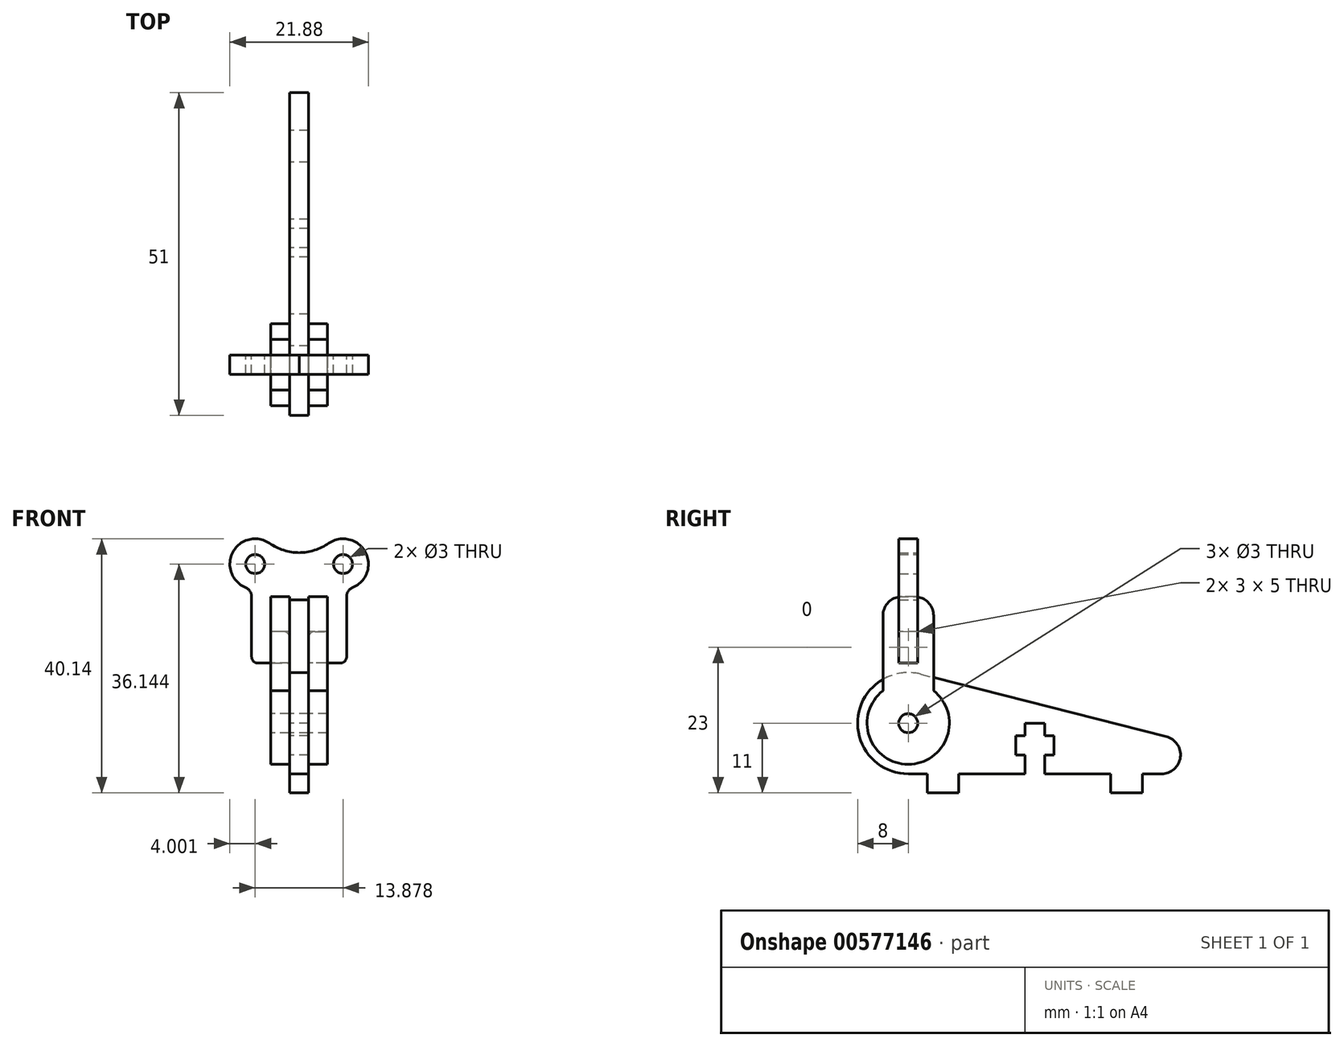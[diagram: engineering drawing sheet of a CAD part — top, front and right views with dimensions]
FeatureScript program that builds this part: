
annotation { "Feature Type Name" : "Feature", "Feature Type Description" : "" }
export const myFeature = defineFeature(function(context is Context, id is Id, definition is map)
    precondition{}
    {
        {
            var Q0;
            Q0=qCreatedBy(makeId("Right.planeOp"),FACE);
            var sketch = newSketch(context, id + "F0", { "sketchPlane" : qUnion([Q0])});
            skLineSegment(sketch, "E0", {"start": v(-20, 0) * mm, "end": v(-17, 0) * mm});
            skLineSegment(sketch, "E1", {"start": v(-17, 0) * mm, "end": v(-17, -3) * mm});
            skLineSegment(sketch, "E2", {"start": v(-17, -3) * mm, "end": v(-12, -3) * mm});
            skLineSegment(sketch, "E3", {"start": v(-12, -3) * mm, "end": v(-12, 0) * mm});
            skLineSegment(sketch, "E4", {"start": v(-12, 0) * mm, "end": v(-1.55, 0) * mm});
            skLineSegment(sketch, "E5", {"start": v(1.55, 0) * mm, "end": v(12, 0) * mm});
            skLineSegment(sketch, "E6", {"start": v(12, 0) * mm, "end": v(12, -3) * mm});
            skLineSegment(sketch, "E7", {"start": v(12, -3) * mm, "end": v(17, -3) * mm});
            skLineSegment(sketch, "E8", {"start": v(17, -3) * mm, "end": v(17, 0) * mm});
            skLineSegment(sketch, "E9", {"start": v(17, 0) * mm, "end": v(20, 0) * mm});
            skLineSegment(sketch, "E10", {"start": v(-1.55, 0) * mm, "end": v(-1.55, 3) * mm});
            skLineSegment(sketch, "E11", {"start": v(-1.55, 3) * mm, "end": v(-3, 3) * mm});
            skLineSegment(sketch, "E12", {"start": v(-3, 3) * mm, "end": v(-3, 6) * mm});
            skLineSegment(sketch, "E13", {"start": v(-3, 6) * mm, "end": v(-1.55, 6) * mm});
            skLineSegment(sketch, "E14", {"start": v(-1.55, 6) * mm, "end": v(-1.55, 8) * mm});
            skLineSegment(sketch, "E15", {"start": v(-1.55, 8) * mm, "end": v(1.55, 8) * mm});
            skLineSegment(sketch, "E16", {"start": v(1.55, 8) * mm, "end": v(1.55, 6) * mm});
            skLineSegment(sketch, "E17", {"start": v(1.55, 6) * mm, "end": v(3, 6) * mm});
            skLineSegment(sketch, "E18", {"start": v(3, 6) * mm, "end": v(3, 3) * mm});
            skLineSegment(sketch, "E19", {"start": v(3, 3) * mm, "end": v(1.55, 3) * mm});
            skLineSegment(sketch, "E20", {"start": v(1.55, 0) * mm, "end": v(1.55, 3) * mm});
            skArc(sketch, "E21", {"start": v(-20, 0) * mm, "mid": v(-27.94, 9) * mm, "end": v(-18.03, 15.75) * mm});
            skCircle(sketch, "E22", {"center": v(-20, 8) * mm, "radius": 1.5 * mm});
            skArc(sketch, "E23", {"start": v(20, 0) * mm, "mid": v(22.98, 2.63) * mm, "end": v(20.74, 5.9) * mm});
            skLineSegment(sketch, "E24", {"start": v(-18.03, 15.75) * mm, "end": v(20.74, 5.9) * mm});
            skSolve(sketch);
        }
        {
            var Q0;
            Q0=qSketchRegion(id+"F0",true);
            extrude(context, id + "F1", {"entities" : qUnion([Q0]), "endBound" : BoundingType.SYMMETRIC, "depth" : 3 * mm});
        }
        {
            var Q0;
            Q0=makeQuery(id+"F1.opExtrude","CAP_FACE",FACE,{"disambiguationData":[OSD([sQuery(id+"F0.wireOp",EDGE,"E0"),sQuery(id+"F0.wireOp",EDGE,"E1"),sQuery(id+"F0.wireOp",EDGE,"E2"),sQuery(id+"F0.wireOp",EDGE,"E3"),sQuery(id+"F0.wireOp",EDGE,"E4"),sQuery(id+"F0.wireOp",EDGE,"E5"),sQuery(id+"F0.wireOp",EDGE,"E6"),sQuery(id+"F0.wireOp",EDGE,"E7"),sQuery(id+"F0.wireOp",EDGE,"E8"),sQuery(id+"F0.wireOp",EDGE,"E9"),sQuery(id+"F0.wireOp",EDGE,"E10"),sQuery(id+"F0.wireOp",EDGE,"E11"),sQuery(id+"F0.wireOp",EDGE,"E12"),sQuery(id+"F0.wireOp",EDGE,"E13"),sQuery(id+"F0.wireOp",EDGE,"E14"),sQuery(id+"F0.wireOp",EDGE,"E15"),sQuery(id+"F0.wireOp",EDGE,"E16"),sQuery(id+"F0.wireOp",EDGE,"E17"),sQuery(id+"F0.wireOp",EDGE,"E18"),sQuery(id+"F0.wireOp",EDGE,"E19"),sQuery(id+"F0.wireOp",EDGE,"E20"),sQuery(id+"F0.wireOp",EDGE,"E21"),sQuery(id+"F0.wireOp",EDGE,"E22"),sQuery(id+"F0.wireOp",EDGE,"E23"),sQuery(id+"F0.wireOp",EDGE,"E24")])],"isStart":false});
            var sketch = newSketch(context, id + "F2", { "sketchPlane" : qUnion([Q0])});
            skCircle(sketch, "E25", {"center": v(-20, 8) * mm, "radius": 1.5 * mm});
            skArc(sketch, "E26.0", {"start": v(-24, 13.12) * mm, "mid": v(-20, 1.5) * mm, "end": v(-16, 13.12) * mm});
            skLineSegment(sketch, "E27", {"start": v(-20, 24.79) * mm, "end": v(-20, -12.76) * mm, "construction": true});
            skLineSegment(sketch, "E28.top", {"start": v(-19, 28) * mm, "end": v(-21, 28) * mm});
            skLineSegment(sketch, "E28.left", {"start": v(-16, 13.12) * mm, "end": v(-16, 25) * mm});
            skLineSegment(sketch, "E28.right", {"start": v(-24, 13.12) * mm, "end": v(-24, 25) * mm});
            skPoint(sketch, "E28.middle", {"position": v(-20, 20.56) * mm});
            skLineSegment(sketch, "E29.bottom", {"start": v(-18.5, 17.5) * mm, "end": v(-21.5, 17.5) * mm});
            skLineSegment(sketch, "E29.top", {"start": v(-18.5, 22.5) * mm, "end": v(-21.5, 22.5) * mm});
            skLineSegment(sketch, "E29.left", {"start": v(-18.5, 17.5) * mm, "end": v(-18.5, 22.5) * mm});
            skLineSegment(sketch, "E29.right", {"start": v(-21.5, 17.5) * mm, "end": v(-21.5, 22.5) * mm});
            skPoint(sketch, "E29.middle", {"position": v(-20, 20) * mm});
            skPoint(sketch, "E30.visualSharp", {"position": v(-24, 28) * mm});
            skArc(sketch, "E30.filletArc", {"start": v(-21, 28) * mm, "mid": v(-23.12, 27.12) * mm, "end": v(-24, 25) * mm});
            skPoint(sketch, "E31.visualSharp", {"position": v(-16, 28) * mm});
            skArc(sketch, "E31.filletArc", {"start": v(-16, 25) * mm, "mid": v(-16.88, 27.12) * mm, "end": v(-19, 28) * mm});
            skSolve(sketch);
        }
        {
            var Q0;
            Q0=qSketchRegion(id+"F2",true);
            extrude(context, id + "F3", {"entities" : qUnion([Q0]), "depth" : 3 * mm});
        }
        {
            var Q0;
            Q0=makeQuery(id+"F3.opExtrude","SWEPT_BODY",BODY,{"disambiguationData":[OSD([sQuery(id+"F2.wireOp",EDGE,"E25"),sQuery(id+"F2.wireOp",EDGE,"E26.0"),sQuery(id+"F2.wireOp",EDGE,"E28.top"),sQuery(id+"F2.wireOp",EDGE,"E28.left"),sQuery(id+"F2.wireOp",EDGE,"E28.right"),sQuery(id+"F2.wireOp",EDGE,"E29.bottom"),sQuery(id+"F2.wireOp",EDGE,"E29.top"),sQuery(id+"F2.wireOp",EDGE,"E29.left"),sQuery(id+"F2.wireOp",EDGE,"E29.right"),sQuery(id+"F2.wireOp",EDGE,"E30.filletArc"),sQuery(id+"F2.wireOp",EDGE,"E31.filletArc")])]});
            transform(context, id + "F4", {"entities" : qUnion([Q0]), "transformType" : TransformType.TRANSLATION_3D, "dx" : -6 * mm, "dy" : 0 * mm, "dz" : 0 * mm, "makeCopy" : true});
        }
        {
            var Q0;
            Q0=makeQuery(id+"F3.opExtrude","SWEPT_FACE",FACE,{"disambiguationData":[OSD([sQuery(id+"F2.wireOp",EDGE,"E29.left")])]});
            var Q1;
            Q1=makeQuery(id+"F3.opExtrude","SWEPT_FACE",FACE,{"disambiguationData":[OSD([sQuery(id+"F2.wireOp",EDGE,"E29.right")])]});
            cPlane(context, id + "F5", {"entities" : qUnion([Q0, Q1]), "cplaneType" : CPlaneType.MID_PLANE, "offset" : 25 * mm, "width" : 150 * mm, "height" : 150 * mm});
        }
        {
            var Q0;
            Q0=qCreatedBy(id+"F5.planeOp",FACE);
            var sketch = newSketch(context, id + "F6", { "sketchPlane" : qUnion([Q0])});
            skLineSegment(sketch, "E32", {"start": v(0, 27.5) * mm, "end": v(-1.5, 27.5) * mm});
            skLineSegment(sketch, "E33", {"start": v(-1.5, 27.5) * mm, "end": v(-1.5, 28) * mm});
            skLineSegment(sketch, "E34", {"start": v(-1.5, 28) * mm, "end": v(-4.5, 28) * mm});
            skLineSegment(sketch, "E35", {"start": v(-7.5, 18.5) * mm, "end": v(-7.5, 28) * mm});
            skArc(sketch, "E36", {"start": v(-7.5, 28) * mm, "mid": v(-7.76, 28.87) * mm, "end": v(-8.47, 29.45) * mm});
            skArc(sketch, "E37", {"start": v(-8.47, 29.45) * mm, "mid": v(-10.45, 35.05) * mm, "end": v(-4.67, 36.44) * mm});
            skCircle(sketch, "E38", {"center": v(-6.94, 33.14) * mm, "radius": 1.5 * mm});
            skLineSegment(sketch, "E39", {"start": v(-6.5, 17.5) * mm, "end": v(-1.5, 17.5) * mm});
            skLineSegment(sketch, "E40", {"start": v(-1.5, 17.5) * mm, "end": v(-1.5, 21.5) * mm});
            skLineSegment(sketch, "E41", {"start": v(-2.5, 22.5) * mm, "end": v(-4.5, 22.5) * mm});
            skLineSegment(sketch, "E42", {"start": v(-4.5, 22.5) * mm, "end": v(-4.5, 28) * mm});
            skPoint(sketch, "E43.visualSharp", {"position": v(-7.5, 17.5) * mm});
            skArc(sketch, "E43.filletArc", {"start": v(-7.5, 18.5) * mm, "mid": v(-7.2, 17.8) * mm, "end": v(-6.5, 17.5) * mm});
            skArc(sketch, "E44", {"start": v(-4.67, 36.44) * mm, "mid": v(-2.44, 35.34) * mm, "end": v(0, 34.94) * mm});
            skArc(sketch, "E45.MirrorCS", {"start": v(4.67, 36.44) * mm, "mid": v(2.44, 35.34) * mm, "end": v(0, 34.94) * mm});
            skArc(sketch, "E46.MirrorCS", {"start": v(8.47, 29.45) * mm, "mid": v(10.45, 35.05) * mm, "end": v(4.67, 36.44) * mm});
            skCircle(sketch, "E47.MirrorC", {"center": v(6.94, 33.14) * mm, "radius": 1.5 * mm});
            skArc(sketch, "E48.MirrorCS", {"start": v(7.5, 28) * mm, "mid": v(7.76, 28.87) * mm, "end": v(8.47, 29.45) * mm});
            skLineSegment(sketch, "E49.MirrorCS", {"start": v(7.5, 18.5) * mm, "end": v(7.5, 28) * mm});
            skArc(sketch, "E50.MirrorCS", {"start": v(7.5, 18.5) * mm, "mid": v(7.2, 17.8) * mm, "end": v(6.5, 17.5) * mm});
            skLineSegment(sketch, "E51.MirrorCS", {"start": v(6.5, 17.5) * mm, "end": v(1.5, 17.5) * mm});
            skLineSegment(sketch, "E52.MirrorCS", {"start": v(1.5, 17.5) * mm, "end": v(1.5, 21.5) * mm});
            skLineSegment(sketch, "E53.MirrorCS", {"start": v(2.5, 22.5) * mm, "end": v(4.5, 22.5) * mm});
            skLineSegment(sketch, "E54.MirrorCS", {"start": v(4.5, 22.5) * mm, "end": v(4.5, 28) * mm});
            skLineSegment(sketch, "E55.MirrorCS", {"start": v(1.5, 28) * mm, "end": v(4.5, 28) * mm});
            skLineSegment(sketch, "E56.MirrorCS", {"start": v(1.5, 27.5) * mm, "end": v(1.5, 28) * mm});
            skLineSegment(sketch, "E57.MirrorCS", {"start": v(0, 27.5) * mm, "end": v(1.5, 27.5) * mm});
            skPoint(sketch, "E58.visualSharp", {"position": v(-1.5, 22.5) * mm});
            skArc(sketch, "E58.filletArc", {"start": v(-1.5, 21.5) * mm, "mid": v(-1.8, 22.2) * mm, "end": v(-2.5, 22.5) * mm});
            skPoint(sketch, "E59.visualSharp", {"position": v(1.5, 22.5) * mm});
            skArc(sketch, "E59.filletArc", {"start": v(2.5, 22.5) * mm, "mid": v(1.8, 22.2) * mm, "end": v(1.5, 21.5) * mm});
            skSolve(sketch);
        }
        {
            var Q0;
            Q0=qSketchRegion(id+"F6",true);
            extrude(context, id + "F7", {"entities" : qUnion([Q0]), "endBound" : BoundingType.SYMMETRIC, "depth" : 3 * mm});
        }
    });
